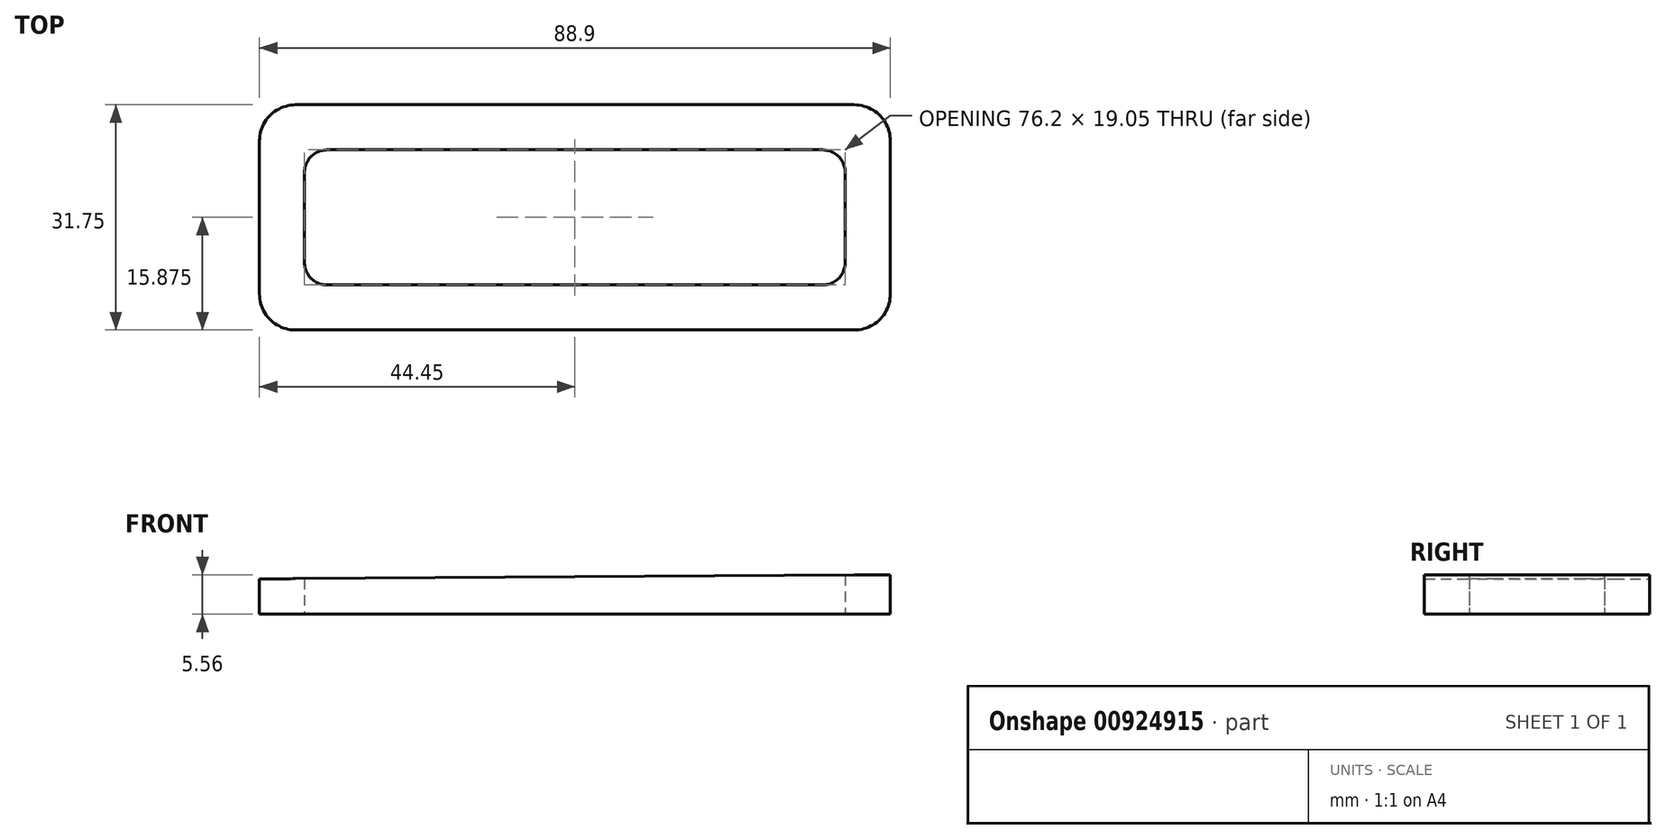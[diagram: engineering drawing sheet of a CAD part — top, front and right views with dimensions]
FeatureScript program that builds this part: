
annotation { "Feature Type Name" : "Feature", "Feature Type Description" : "" }
export const myFeature = defineFeature(function(context is Context, id is Id, definition is map)
    precondition{}
    {
        {
            var Q0;
            Q0=qCreatedBy(makeId("Front.planeOp"),FACE);
            var sketch = newSketch(context, id + "F0", { "sketchPlane" : qUnion([Q0])});
            skLineSegment(sketch, "E0", {"start": v(0, 0) * mm, "end": v(0, 1.59) * mm});
            skLineSegment(sketch, "E1", {"start": v(0, 1.59) * mm, "end": v(609.6, 5.56) * mm});
            skLineSegment(sketch, "E2", {"start": v(609.6, 5.56) * mm, "end": v(609.6, 0) * mm});
            skLineSegment(sketch, "E3", {"start": v(609.6, 0) * mm, "end": v(0, 0) * mm});
            skSolve(sketch);
        }
        {
            var Q0;
            Q0=qCreatedBy(makeId("Front.planeOp"),FACE);
            var sketch = newSketch(context, id + "F1", { "sketchPlane" : qUnion([Q0])});
            skLineSegment(sketch, "E4", {"start": v(609.6, 5.56) * mm, "end": v(520.7, 4.98) * mm});
            skLineSegment(sketch, "E5", {"start": v(520.7, 4.98) * mm, "end": v(520.7, 0) * mm});
            skLineSegment(sketch, "E6", {"start": v(520.7, 0) * mm, "end": v(609.6, 0) * mm});
            skLineSegment(sketch, "E7", {"start": v(609.6, 0) * mm, "end": v(609.6, 5.56) * mm});
            skSolve(sketch);
        }
        {
            var Q0;
            Q0=qCreatedBy(makeId("Front.planeOp"),FACE);
            var sketch = newSketch(context, id + "F2", { "sketchPlane" : qUnion([Q0])});
            skLineSegment(sketch, "E8", {"start": v(444.5, 4.48) * mm, "end": v(444.5, 0) * mm});
            skLineSegment(sketch, "E9", {"start": v(444.5, 0) * mm, "end": v(355.6, 0) * mm});
            skLineSegment(sketch, "E10", {"start": v(-243.84, 0) * mm, "end": v(-243.84, 0) * mm});
            skLineSegment(sketch, "E11", {"start": v(355.57, 3.9) * mm, "end": v(444.5, 4.48) * mm});
            skLineSegment(sketch, "E12", {"start": v(355.57, 3.9) * mm, "end": v(355.6, 0) * mm});
            skSolve(sketch);
        }
        {
            var Q0;
            Q0 = qSketchRegion(id + "F1", true);
            extrude(context, id + "F3", {"entities" : qUnion([Q0]), "depth" : 31.75 * mm, "offsetDistance" : 25.4 * mm});
        }
        {
            var Q0;
            Q0=makeQuery(id+"F3.opExtrude","SWEPT_FACE",FACE,{"disambiguationData":[OSD([sQuery(id+"F1.wireOp",EDGE,"E6")])]});
            var sketch = newSketch(context, id + "F4", { "sketchPlane" : qUnion([Q0])});
            skLineSegment(sketch, "E13.bottom", {"start": v(530.23, 25.4) * mm, "end": v(600.08, 25.4) * mm});
            skLineSegment(sketch, "E13.top", {"start": v(530.23, 6.35) * mm, "end": v(600.08, 6.35) * mm});
            skLineSegment(sketch, "E13.left", {"start": v(527.05, 22.22) * mm, "end": v(527.05, 9.52) * mm});
            skLineSegment(sketch, "E13.right", {"start": v(603.25, 22.23) * mm, "end": v(603.25, 9.53) * mm});
            skPoint(sketch, "E14.visualSharp", {"position": v(527.05, 25.4) * mm});
            skArc(sketch, "E14.filletArc", {"start": v(530.23, 25.4) * mm, "mid": v(527.98, 24.47) * mm, "end": v(527.05, 22.22) * mm});
            skPoint(sketch, "E15.visualSharp", {"position": v(527.05, 6.35) * mm});
            skArc(sketch, "E15.filletArc", {"start": v(527.05, 9.52) * mm, "mid": v(527.98, 7.28) * mm, "end": v(530.23, 6.35) * mm});
            skPoint(sketch, "E16.visualSharp", {"position": v(603.25, 6.35) * mm});
            skArc(sketch, "E16.filletArc", {"start": v(600.08, 6.35) * mm, "mid": v(602.32, 7.28) * mm, "end": v(603.25, 9.53) * mm});
            skPoint(sketch, "E17.visualSharp", {"position": v(603.25, 25.4) * mm});
            skArc(sketch, "E17.filletArc", {"start": v(603.25, 22.23) * mm, "mid": v(602.32, 24.47) * mm, "end": v(600.08, 25.4) * mm});
            skSolve(sketch);
        }
        {
            var Q0;
            Q0 = qSketchRegion(id + "F4", true);
            extrude(context, id + "F5", {"entities" : qUnion([Q0]), "operationType" : NewBodyOperationType.REMOVE, "endBound" : BoundingType.THROUGH_ALL, "oppositeDirection" : true, "depth" : 25.4 * mm, "offsetDistance" : 25.4 * mm});
        }
        {
            var Q0;
            Q0=makeQuery(id+"F3.opExtrude","CAP_EDGE",EDGE,{"disambiguationData":[OSD([sQuery(id+"F1.wireOp",EDGE,"E5")])],"isStart":false});
            var Q1;
            Q1=makeQuery(id+"F3.opExtrude","CAP_EDGE",EDGE,{"disambiguationData":[OSD([sQuery(id+"F1.wireOp",EDGE,"E5")])],"isStart":true});
            var Q2;
            Q2=makeQuery(id+"F3.opExtrude","CAP_EDGE",EDGE,{"disambiguationData":[OSD([sQuery(id+"F1.wireOp",EDGE,"E7")])],"isStart":false});
            var Q3;
            Q3=makeQuery(id+"F3.opExtrude","CAP_EDGE",EDGE,{"disambiguationData":[OSD([sQuery(id+"F1.wireOp",EDGE,"E7")])],"isStart":true});
            fillet(context, id + "F6", {"entities" : qUnion([Q0, Q1, Q2, Q3]), "radius" : 5.08 * mm, "tangentPropagation" : true, "allowEdgeOverflow" : false});
        }
    });
